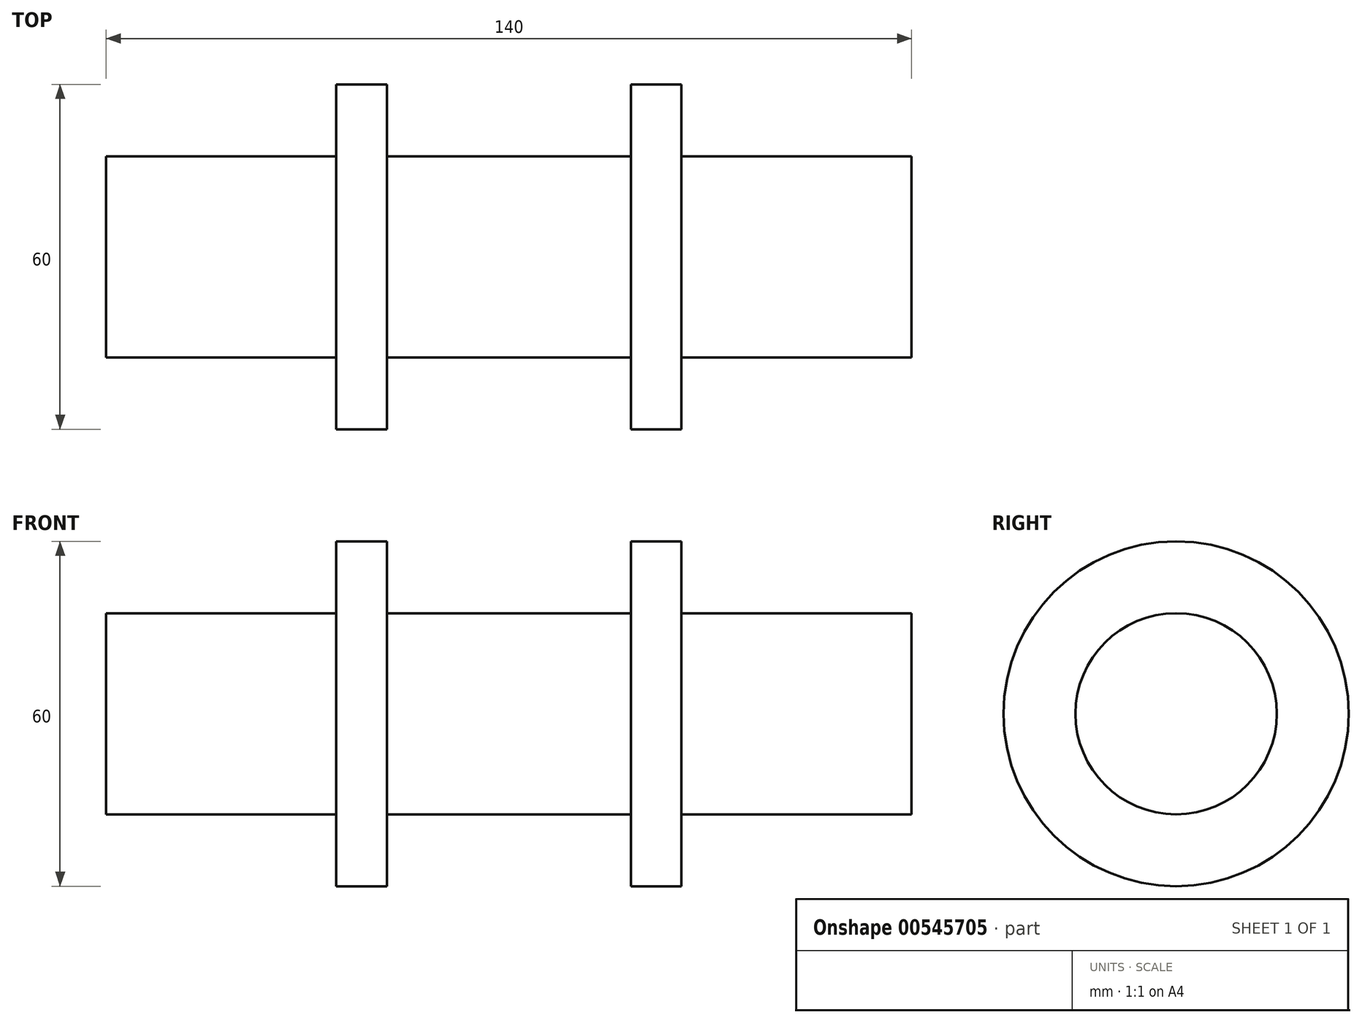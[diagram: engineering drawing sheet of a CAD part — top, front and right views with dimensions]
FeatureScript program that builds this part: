
annotation { "Feature Type Name" : "Feature", "Feature Type Description" : "" }
export const myFeature = defineFeature(function(context is Context, id is Id, definition is map)
    precondition{}
    {
        {
            var Q0;
            Q0=qCreatedBy(makeId("Front.planeOp"),FACE);
            var sketch = newSketch(context, id + "F0", { "sketchPlane" : qUnion([Q0])});
            skLineSegment(sketch, "E0", {"start": v(70, 0) * mm, "end": v(70, 17.5) * mm});
            skLineSegment(sketch, "E1", {"start": v(70, 17.5) * mm, "end": v(30, 17.5) * mm});
            skLineSegment(sketch, "E2", {"start": v(30, 17.5) * mm, "end": v(30, 30) * mm});
            skLineSegment(sketch, "E3", {"start": v(30, 30) * mm, "end": v(21.22, 30) * mm});
            skLineSegment(sketch, "E4", {"start": v(21.22, 30) * mm, "end": v(21.22, 17.5) * mm});
            skLineSegment(sketch, "E5", {"start": v(21.22, 17.5) * mm, "end": v(0, 17.5) * mm});
            skLineSegment(sketch, "E6", {"start": v(0, 17.5) * mm, "end": v(0, 0) * mm});
            skLineSegment(sketch, "E7", {"start": v(0, 0) * mm, "end": v(70, 0) * mm});
            skSolve(sketch);
        }
        {
            var Q0;
            Q0=makeQuery(id+"F0.imprint","IMPRINT",FACE,{"disambiguationData":[TD([[makeQuery(id+"F0.imprint","IMPRINT",EDGE,{"derivedFrom":sQuery(id+"F0.wireOp",EDGE,"E0")}),1.0]])]});
            var Q1;
            Q1=sQuery(id+"F0.wireOp",EDGE,"E7");
            revolve(context, id + "F1", {"entities" : qUnion([Q0]), "axis" : qUnion([Q1]), "revolveType" : RevolveType.FULL});
        }
        {
            var Q0;
            Q0=makeQuery(id+"F1.opRevolve","SWEPT_BODY",BODY,{"disambiguationData":[OSD([sQuery(id+"F0.wireOp",EDGE,"E0"),sQuery(id+"F0.wireOp",EDGE,"E1"),sQuery(id+"F0.wireOp",EDGE,"E2"),sQuery(id+"F0.wireOp",EDGE,"E3"),sQuery(id+"F0.wireOp",EDGE,"E4"),sQuery(id+"F0.wireOp",EDGE,"E5"),sQuery(id+"F0.wireOp",EDGE,"E6"),sQuery(id+"F0.wireOp",EDGE,"E7")])]});
            var Q1;
            Q1=qCreatedBy(makeId("Right.planeOp"),FACE);
            mirror(context, id + "F2", {"operationType" : NewBodyOperationType.ADD, "entities" : qUnion([Q0]), "mirrorPlane" : qUnion([Q1])});
        }
    });
